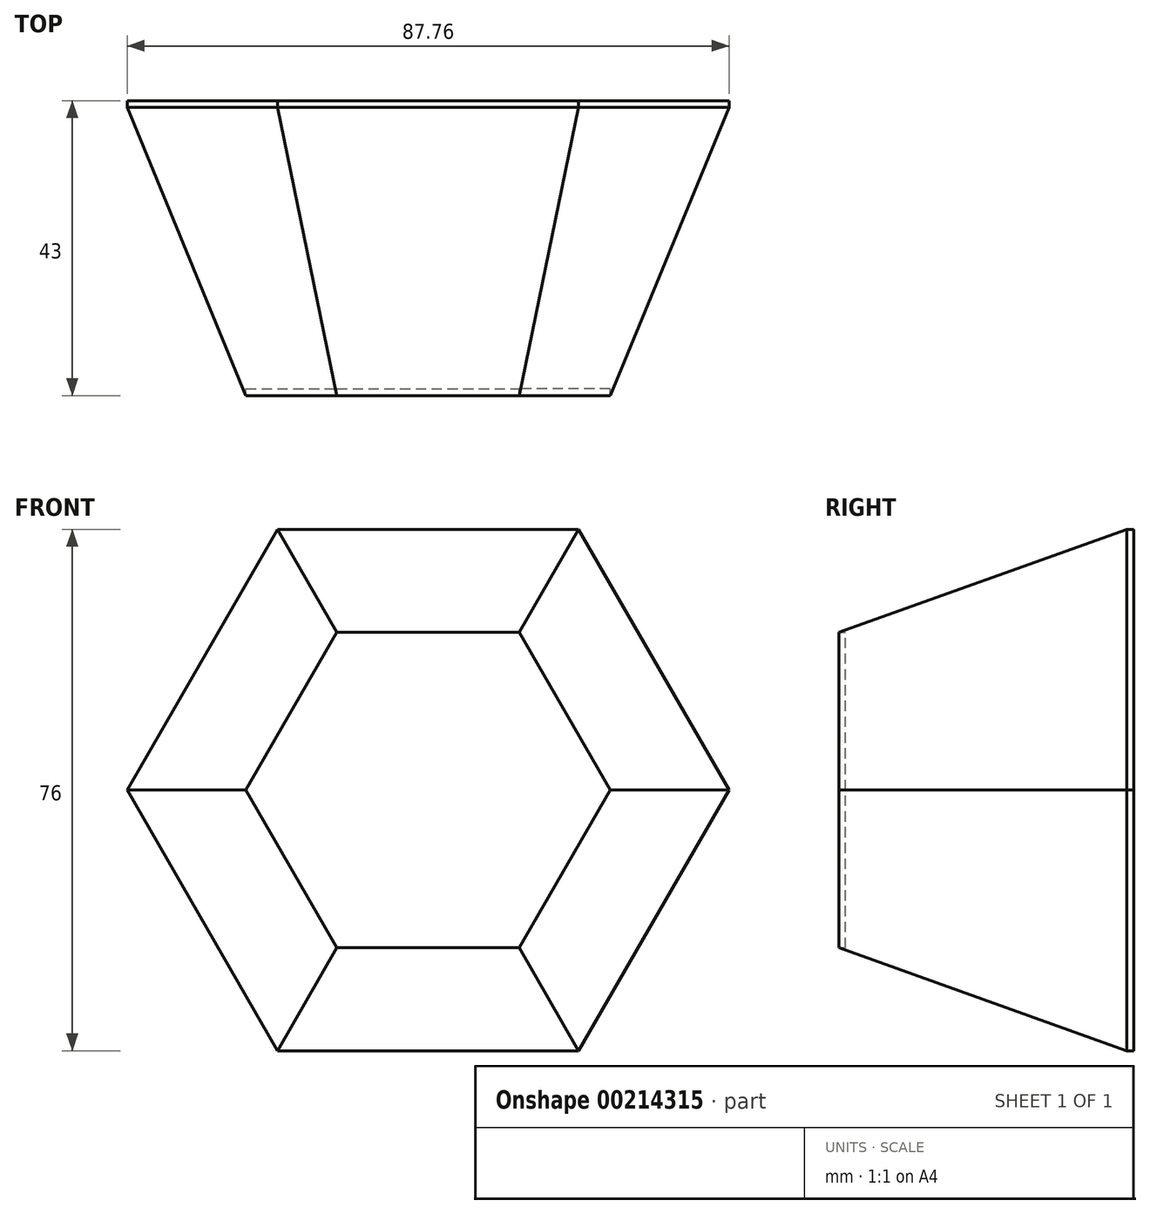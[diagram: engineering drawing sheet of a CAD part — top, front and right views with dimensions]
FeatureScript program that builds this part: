
annotation { "Feature Type Name" : "Feature", "Feature Type Description" : "" }
export const myFeature = defineFeature(function(context is Context, id is Id, definition is map)
    precondition{}
    {
        {
            var Q0;
            Q0=qCreatedBy(makeId("Front.planeOp"),FACE);
            var sketch = newSketch(context, id + "F0", { "sketchPlane" : qUnion([Q0])});
            skCircle(sketch, "E0", {"center": v(0, 0) * mm, "radius": 38 * mm});
            skCircle(sketch, "E1.cCircle", {"center": v(0, 0) * mm, "radius": 38 * mm, "construction": true});
            skLineSegment(sketch, "E1.0", {"start": v(-21.94, 38) * mm, "end": v(21.94, 38) * mm});
            skLineSegment(sketch, "E1.1", {"start": v(21.94, 38) * mm, "end": v(43.88, 0) * mm});
            skLineSegment(sketch, "E1.2", {"start": v(43.88, 0) * mm, "end": v(21.94, -38) * mm});
            skLineSegment(sketch, "E1.3", {"start": v(21.94, -38) * mm, "end": v(-21.94, -38) * mm});
            skLineSegment(sketch, "E1.4", {"start": v(-21.94, -38) * mm, "end": v(-43.88, 0) * mm});
            skLineSegment(sketch, "E1.5", {"start": v(-43.88, 0) * mm, "end": v(-21.94, 38) * mm});
            skPoint(sketch, "E1.0.midPoint", {"position": v(0, 38) * mm});
            skSolve(sketch);
        }
        {
            var Q0;
            Q0 = qSketchRegion(id + "F0", true);
            extrude(context, id + "F1", {"entities" : qUnion([Q0]), "depth" : 1 * mm, "offsetDistance" : 25 * mm});
        }
        {
            var Q0;
            Q0=qCreatedBy(makeId("Front.planeOp"),FACE);
            cPlane(context, id + "F2", {"entities" : qUnion([Q0]), "cplaneType" : CPlaneType.OFFSET, "offset" : 42 * mm, "width" : 150 * mm, "height" : 150 * mm});
        }
        {
            var Q0;
            Q0=qCreatedBy(id+"F2.planeOp",FACE);
            var sketch = newSketch(context, id + "F3", { "sketchPlane" : qUnion([Q0])});
            skCircle(sketch, "E2.cCircle", {"center": v(0, 0) * mm, "radius": 23 * mm, "construction": true});
            skLineSegment(sketch, "E2.0", {"start": v(-13.28, 23) * mm, "end": v(13.28, 23) * mm});
            skLineSegment(sketch, "E2.1", {"start": v(13.28, 23) * mm, "end": v(26.56, 0) * mm});
            skLineSegment(sketch, "E2.2", {"start": v(26.56, 0) * mm, "end": v(13.28, -23) * mm});
            skLineSegment(sketch, "E2.3", {"start": v(13.28, -23) * mm, "end": v(-13.28, -23) * mm});
            skLineSegment(sketch, "E2.4", {"start": v(-13.28, -23) * mm, "end": v(-26.56, 0) * mm});
            skLineSegment(sketch, "E2.5", {"start": v(-26.56, 0) * mm, "end": v(-13.28, 23) * mm});
            skPoint(sketch, "E2.0.midPoint", {"position": v(0, 23) * mm});
            skSolve(sketch);
        }
        {
            var Q0;
            Q0 = qSketchRegion(id + "F3", true);
            extrude(context, id + "F4", {"entities" : qUnion([Q0]), "depth" : 1 * mm, "offsetDistance" : 25 * mm});
        }
        {
            var Q0;
            Q0=makeQuery(id+"F1.opExtrude","CAP_FACE",FACE,{"disambiguationData":[OSD([sQuery(id+"F0.wireOp",EDGE,"E1.0"),sQuery(id+"F0.wireOp",EDGE,"E1.1"),sQuery(id+"F0.wireOp",EDGE,"E1.2"),sQuery(id+"F0.wireOp",EDGE,"E1.3"),sQuery(id+"F0.wireOp",EDGE,"E1.4"),sQuery(id+"F0.wireOp",EDGE,"E1.5")])],"isStart":false});
            var sketch = newSketch(context, id + "F5", { "sketchPlane" : qUnion([Q0])});
            skCircle(sketch, "E3.cCircle", {"center": v(0, 0) * mm, "radius": 38 * mm, "construction": true});
            skLineSegment(sketch, "E3.0", {"start": v(-21.94, 38) * mm, "end": v(21.94, 38) * mm});
            skLineSegment(sketch, "E3.1", {"start": v(21.94, 38) * mm, "end": v(43.88, 0) * mm});
            skLineSegment(sketch, "E3.2", {"start": v(43.88, 0) * mm, "end": v(21.94, -38) * mm});
            skLineSegment(sketch, "E3.3", {"start": v(21.94, -38) * mm, "end": v(-21.94, -38) * mm});
            skLineSegment(sketch, "E3.4", {"start": v(-21.94, -38) * mm, "end": v(-43.88, 0) * mm});
            skLineSegment(sketch, "E3.5", {"start": v(-43.88, 0) * mm, "end": v(-21.94, 38) * mm});
            skPoint(sketch, "E3.0.midPoint", {"position": v(0, 38) * mm});
            skSolve(sketch);
        }
        {
            var Q0;
            Q0=makeQuery(id+"F4.opExtrude","CAP_FACE",FACE,{"disambiguationData":[OSD([sQuery(id+"F3.wireOp",EDGE,"E2.0"),sQuery(id+"F3.wireOp",EDGE,"E2.1"),sQuery(id+"F3.wireOp",EDGE,"E2.2"),sQuery(id+"F3.wireOp",EDGE,"E2.3"),sQuery(id+"F3.wireOp",EDGE,"E2.4"),sQuery(id+"F3.wireOp",EDGE,"E2.5")])],"isStart":false});
            var sketch = newSketch(context, id + "F6", { "sketchPlane" : qUnion([Q0])});
            skCircle(sketch, "E4.cCircle", {"center": v(0, 0) * mm, "radius": 23 * mm, "construction": true});
            skLineSegment(sketch, "E4.0", {"start": v(-13.28, 23) * mm, "end": v(13.28, 23) * mm});
            skLineSegment(sketch, "E4.1", {"start": v(13.28, 23) * mm, "end": v(26.56, 0) * mm});
            skLineSegment(sketch, "E4.2", {"start": v(26.56, 0) * mm, "end": v(13.28, -23) * mm});
            skLineSegment(sketch, "E4.3", {"start": v(13.28, -23) * mm, "end": v(-13.28, -23) * mm});
            skLineSegment(sketch, "E4.4", {"start": v(-13.28, -23) * mm, "end": v(-26.56, 0) * mm});
            skLineSegment(sketch, "E4.5", {"start": v(-26.56, 0) * mm, "end": v(-13.28, 23) * mm});
            skPoint(sketch, "E4.0.midPoint", {"position": v(0, 23) * mm});
            skSolve(sketch);
        }
        {
            var Q0;
            Q0 = qSketchRegion(id + "F5", true);
            var Q1;
            Q1 = qSketchRegion(id + "F6", true);
            loft(context, id + "F7", {"sheetProfilesArray" : [{ "sheetProfileEntities" : qUnion([Q0]) }, { "sheetProfileEntities" : qUnion([Q1]) }]});
        }
    });
